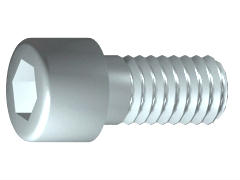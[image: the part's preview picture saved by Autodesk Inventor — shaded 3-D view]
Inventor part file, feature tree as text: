
AUTODESK INVENTOR PART (.ipt)
format: ipt  version: unknown  size: 297,984 bytes
history: native  units: mm (DEFAULTED — no unit token found)
features: extrude x1, plane x1, fillet x1
ambient origin geometry x7: Origin, YZ Plane, XY Plane, X Axis, Y Axis, Z Axis, Center Point
bodies: Solid1 (feature_tree), Body (feature_tree)
feature tree (3):
  extrude  "Slot"  Depth=11.509048mm
  plane  "Work Plane1"
  fillet  "Fillet2"  Radius=1.190852mm
